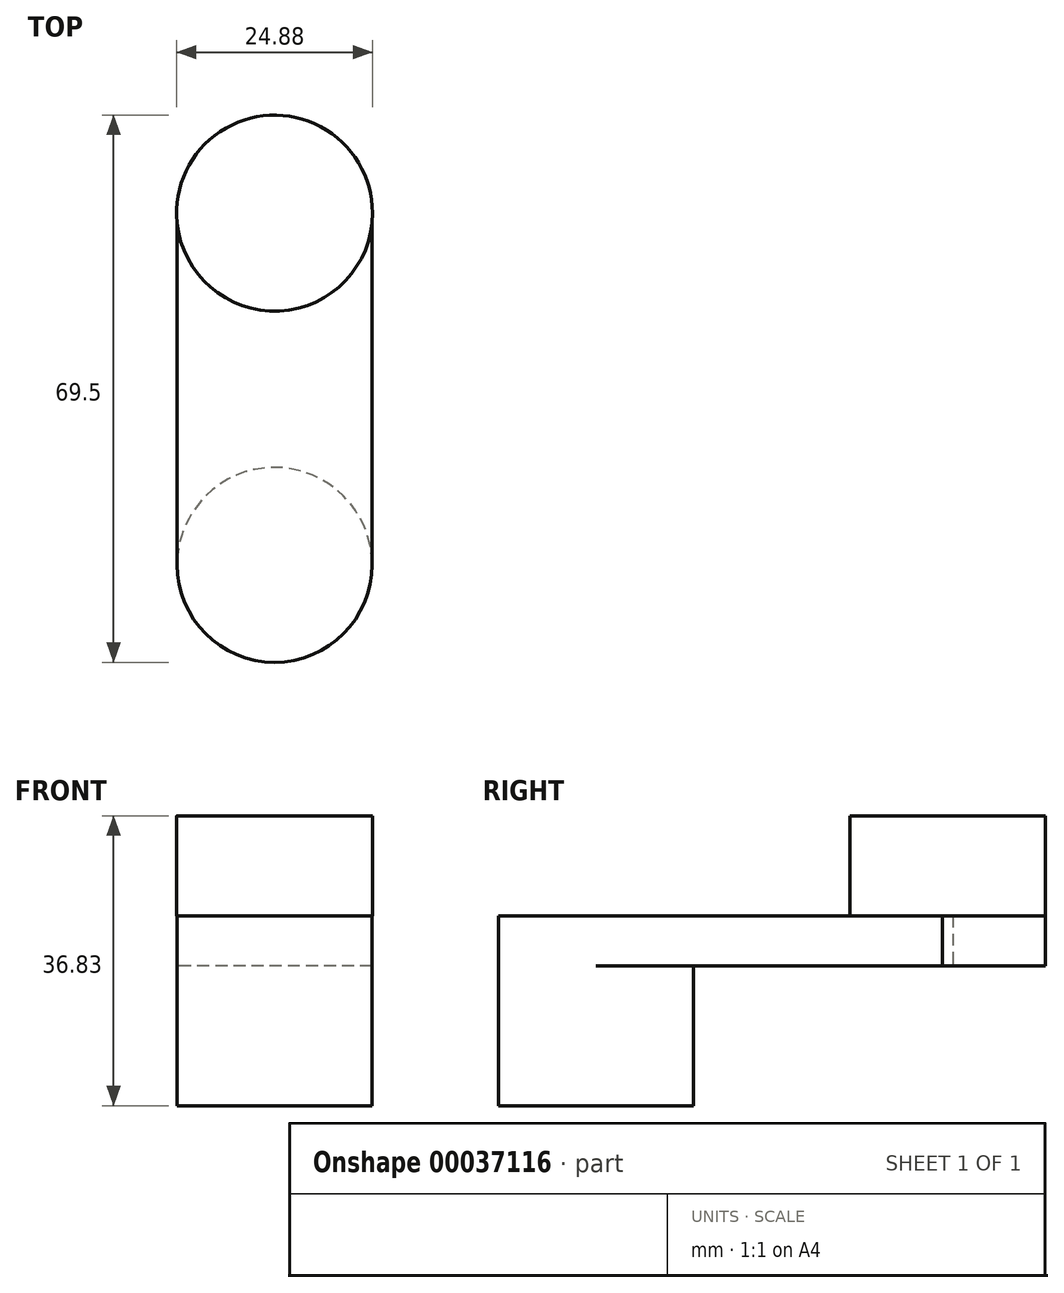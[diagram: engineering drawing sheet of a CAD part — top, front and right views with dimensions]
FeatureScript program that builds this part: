
annotation { "Feature Type Name" : "Feature", "Feature Type Description" : "" }
export const myFeature = defineFeature(function(context is Context, id is Id, definition is map)
    precondition{}
    {
        {
            var Q0;
            Q0=qCreatedBy(makeId("Top.planeOp"),FACE);
            var sketch = newSketch(context, id + "F0", { "sketchPlane" : qUnion([Q0])});
            skCircle(sketch, "E0", {"center": v(0, 0) * mm, "radius": 12.38 * mm});
            skSolve(sketch);
        }
        {
            var Q0;
            Q0 = qSketchRegion(id + "F0", true);
            extrude(context, id + "F1", {"entities" : qUnion([Q0]), "depth" : 17.78 * mm});
        }
        {
            var Q0;
            Q0=makeQuery(id+"F1.opExtrude","CAP_FACE",FACE,{"disambiguationData":[OSD([sQuery(id+"F0.wireOp",EDGE,"E0")])],"isStart":false});
            var sketch = newSketch(context, id + "F2", { "sketchPlane" : qUnion([Q0])});
            skArc(sketch, "E1", {"start": v(-12.38, 0) * mm, "mid": v(0, -12.38) * mm, "end": v(12.38, 0) * mm});
            skLineSegment(sketch, "E2", {"start": v(-12.38, 0) * mm, "end": v(-12.38, 45.37) * mm});
            skLineSegment(sketch, "E3", {"start": v(12.38, 0) * mm, "end": v(12.38, 44) * mm});
            skLineSegment(sketch, "E4", {"start": v(-12.38, 45.37) * mm, "end": v(12.38, 44) * mm});
            skArc(sketch, "E5", {"start": v(12.38, 44) * mm, "mid": v(0.7, 57.1) * mm, "end": v(-12.38, 45.37) * mm});
            skSolve(sketch);
        }
        {
            var Q0;
            Q0 = qSketchRegion(id + "F2", true);
            extrude(context, id + "F3", {"entities" : qUnion([Q0]), "operationType" : NewBodyOperationType.ADD, "depth" : 6.35 * mm});
        }
        {
            var Q0;
            Q0=makeQuery(id+"F3.opExtrude","CAP_FACE",FACE,{"disambiguationData":[OSD([sQuery(id+"F2.wireOp",EDGE,"E1"),sQuery(id+"F2.wireOp",EDGE,"E2"),sQuery(id+"F2.wireOp",EDGE,"E3"),sQuery(id+"F2.wireOp",EDGE,"c44713a0-eceb-4721-9d55-e2d2a199089b")])],"isStart":false});
            var sketch = newSketch(context, id + "F4", { "sketchPlane" : qUnion([Q0])});
            skPoint(sketch, "E6", {"position": v(0, 0) * mm});
            skLineSegment(sketch, "E7", {"start": v(-12.38, 45.37) * mm, "end": v(12.38, 44) * mm});
            skPoint(sketch, "E8", {"position": v(0, 44.68) * mm});
            skCircle(sketch, "E9", {"center": v(0, 44.68) * mm, "radius": 12.44 * mm});
            skSolve(sketch);
        }
        {
            var Q0;
            Q0 = qSketchRegion(id + "F4", true);
            extrude(context, id + "F5", {"entities" : qUnion([Q0]), "operationType" : NewBodyOperationType.ADD, "depth" : 12.7 * mm});
        }
    });
